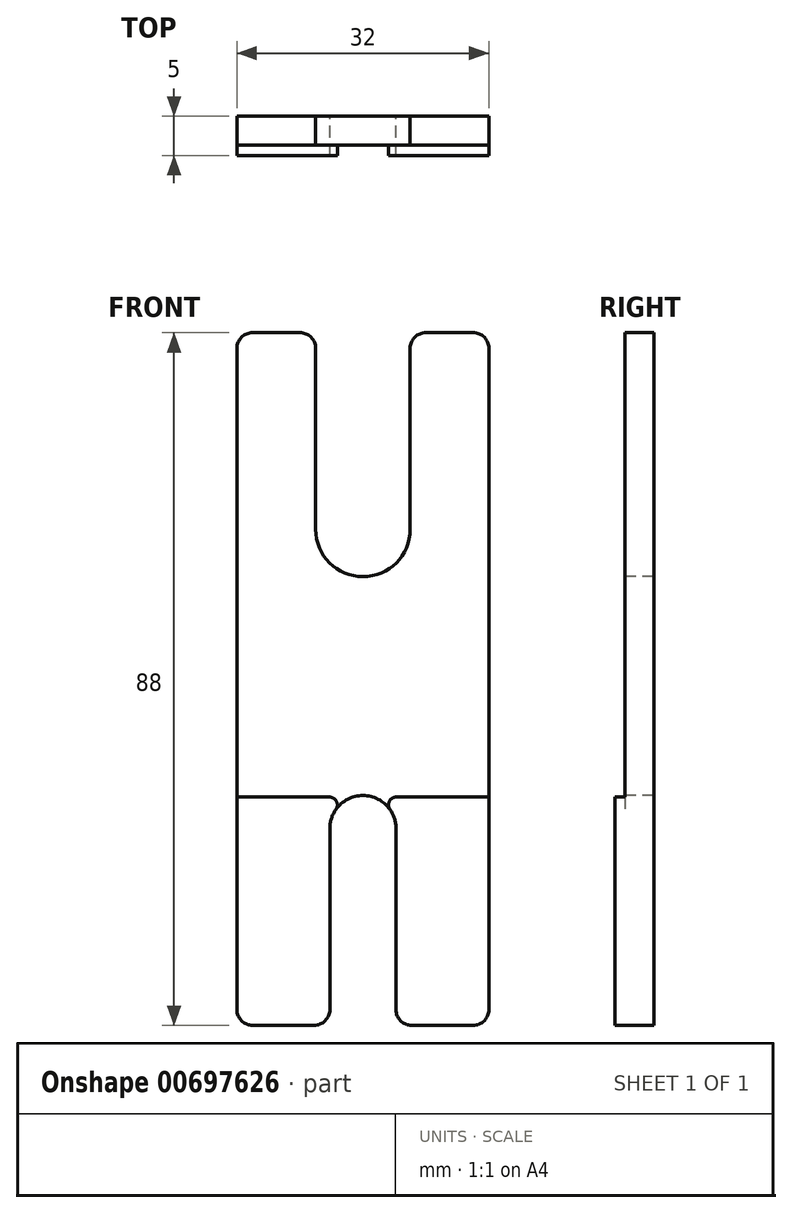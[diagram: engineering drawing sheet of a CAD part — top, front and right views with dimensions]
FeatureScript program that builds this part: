
annotation { "Feature Type Name" : "Feature", "Feature Type Description" : "" }
export const myFeature = defineFeature(function(context is Context, id is Id, definition is map)
    precondition{}
    {
        {
            var Q0;
            Q0=qCreatedBy(makeId("Front.planeOp"),FACE);
            cPlane(context, id + "F0", {"entities" : qUnion([Q0]), "cplaneType" : CPlaneType.OFFSET, "offset" : 13 * mm, "width" : 150 * mm, "height" : 150 * mm});
        }
        {
            var Q0;
            Q0=qCreatedBy(id+"F0.planeOp",FACE);
            var sketch = newSketch(context, id + "F1", { "sketchPlane" : qUnion([Q0])});
            skLineSegment(sketch, "E0.bottom", {"start": v(7, 75) * mm, "end": v(17, 75) * mm});
            skLineSegment(sketch, "E0.top", {"start": v(7, -13) * mm, "end": v(18.8, -13) * mm});
            skLineSegment(sketch, "E0.left", {"start": v(7, 75) * mm, "end": v(7, -13) * mm});
            skLineSegment(sketch, "E0.right", {"start": v(39, 75) * mm, "end": v(39, -13) * mm});
            skLineSegment(sketch, "E1", {"start": v(23, 75) * mm, "end": v(23, -13) * mm, "construction": true});
            skLineSegment(sketch, "E2", {"start": v(7, 31) * mm, "end": v(39, 31) * mm, "construction": true});
            skLineSegment(sketch, "E3", {"start": v(17, 75) * mm, "end": v(17, 50) * mm});
            skLineSegment(sketch, "E4", {"start": v(17, 50) * mm, "end": v(29, 50) * mm});
            skLineSegment(sketch, "E5", {"start": v(29, 50) * mm, "end": v(29, 75) * mm});
            skLineSegment(sketch, "E6", {"start": v(18.8, -13) * mm, "end": v(18.8, 12) * mm});
            skLineSegment(sketch, "E7", {"start": v(18.8, 12) * mm, "end": v(27.2, 12) * mm});
            skLineSegment(sketch, "E8", {"start": v(27.2, 12) * mm, "end": v(27.2, -13) * mm});
            skLineSegment(sketch, "E9.trimOffspring", {"start": v(27.2, -13) * mm, "end": v(39, -13) * mm});
            skLineSegment(sketch, "E10.trimOffspring", {"start": v(29, 75) * mm, "end": v(39, 75) * mm});
            skSolve(sketch);
        }
        {
            var Q0;
            Q0 = qSketchRegion(id + "F1", true);
            extrude(context, id + "F2", {"entities" : qUnion([Q0]), "depth" : (4 + 1) * mm, "offsetDistance" : 25 * mm});
        }
        {
            var Q0;
            Q0=makeQuery(id+"F2.opExtrude","CAP_FACE",FACE,{"disambiguationData":[OSD([sQuery(id+"F1.wireOp",EDGE,"E0.bottom"),sQuery(id+"F1.wireOp",EDGE,"E0.top"),sQuery(id+"F1.wireOp",EDGE,"E0.left"),sQuery(id+"F1.wireOp",EDGE,"E0.right"),sQuery(id+"F1.wireOp",EDGE,"E3"),sQuery(id+"F1.wireOp",EDGE,"E4"),sQuery(id+"F1.wireOp",EDGE,"E5"),sQuery(id+"F1.wireOp",EDGE,"E6"),sQuery(id+"F1.wireOp",EDGE,"E7"),sQuery(id+"F1.wireOp",EDGE,"E8"),sQuery(id+"F1.wireOp",EDGE,"E9.trimOffspring"),sQuery(id+"F1.wireOp",EDGE,"E10.trimOffspring")])],"isStart":false});
            cPlane(context, id + "F3", {"entities" : qUnion([Q0]), "cplaneType" : CPlaneType.OFFSET, "offset" : 0 * mm, "width" : 150 * mm, "height" : 150 * mm});
        }
        {
            var Q0;
            Q0=qCreatedBy(id+"F3.planeOp",FACE);
            var sketch = newSketch(context, id + "F4", { "sketchPlane" : qUnion([Q0])});
            skLineSegment(sketch, "E11.0.2", {"start": v(39, 16) * mm, "end": v(39, 75) * mm});
            skLineSegment(sketch, "E11.0.3", {"start": v(39, 75) * mm, "end": v(29, 75) * mm});
            skLineSegment(sketch, "E11.0.4", {"start": v(29, 75) * mm, "end": v(29, 50) * mm});
            skLineSegment(sketch, "E11.0.5", {"start": v(29, 50) * mm, "end": v(17, 50) * mm});
            skLineSegment(sketch, "E11.0.6", {"start": v(17, 50) * mm, "end": v(17, 75) * mm});
            skLineSegment(sketch, "E11.0.7", {"start": v(17, 75) * mm, "end": v(7, 75) * mm});
            skLineSegment(sketch, "E11.0.8", {"start": v(7, 75) * mm, "end": v(7, 16) * mm});
            skLineSegment(sketch, "E12", {"start": v(7, 16) * mm, "end": v(39, 16) * mm});
            skSolve(sketch);
        }
        {
            var Q0;
            Q0 = qSketchRegion(id + "F4", true);
            extrude(context, id + "F5", {"entities" : qUnion([Q0]), "operationType" : NewBodyOperationType.REMOVE, "oppositeDirection" : true, "depth" : (0.8 + 0.5) * mm, "offsetDistance" : 25 * mm});
        }
        {
            var Q0;
            Q0=makeQuery(id+"F2.opExtrude","CAP_FACE",FACE,{"disambiguationData":[OSD([sQuery(id+"F1.wireOp",EDGE,"E0.bottom"),sQuery(id+"F1.wireOp",EDGE,"E0.top"),sQuery(id+"F1.wireOp",EDGE,"E0.left"),sQuery(id+"F1.wireOp",EDGE,"E0.right"),sQuery(id+"F1.wireOp",EDGE,"E3"),sQuery(id+"F1.wireOp",EDGE,"E4"),sQuery(id+"F1.wireOp",EDGE,"E5"),sQuery(id+"F1.wireOp",EDGE,"E6"),sQuery(id+"F1.wireOp",EDGE,"E7"),sQuery(id+"F1.wireOp",EDGE,"E8"),sQuery(id+"F1.wireOp",EDGE,"E9.trimOffspring"),sQuery(id+"F1.wireOp",EDGE,"E10.trimOffspring")])],"isStart":false});
            cPlane(context, id + "F6", {"entities" : qUnion([Q0]), "cplaneType" : CPlaneType.OFFSET, "offset" : 0 * mm, "width" : 150 * mm, "height" : 150 * mm});
        }
        {
            var Q0;
            Q0=qCreatedBy(id+"F6.planeOp",FACE);
            var sketch = newSketch(context, id + "F7", { "sketchPlane" : qUnion([Q0])});
            skCircle(sketch, "E13", {"center": v(23, 50) * mm, "radius": 6 * mm});
            skCircle(sketch, "E14", {"center": v(23, 12) * mm, "radius": 4.2 * mm});
            skSolve(sketch);
        }
        {
            var Q0;
            Q0 = qSketchRegion(id + "F7", true);
            extrude(context, id + "F8", {"entities" : qUnion([Q0]), "operationType" : NewBodyOperationType.REMOVE, "endBound" : BoundingType.THROUGH_ALL, "oppositeDirection" : true, "depth" : 25 * mm, "offsetDistance" : 25 * mm});
        }
        {
            var Q0;
            Q0=makeQuery(id+"F2.opExtrude","SWEPT_EDGE",EDGE,{"disambiguationData":[OSD([sQuery(id+"F1.wireOp",EDGE,"E0.bottom"),sQuery(id+"F1.wireOp",EDGE,"E0.left")])]});
            var Q1;
            Q1=makeQuery(id+"F2.opExtrude","SWEPT_EDGE",EDGE,{"disambiguationData":[OSD([sQuery(id+"F1.wireOp",EDGE,"E0.bottom"),sQuery(id+"F1.wireOp",EDGE,"E3")])]});
            var Q2;
            Q2=makeQuery(id+"F2.opExtrude","SWEPT_EDGE",EDGE,{"disambiguationData":[OSD([sQuery(id+"F1.wireOp",EDGE,"E5"),sQuery(id+"F1.wireOp",EDGE,"E10.trimOffspring")])]});
            var Q3;
            Q3=makeQuery(id+"F2.opExtrude","SWEPT_EDGE",EDGE,{"disambiguationData":[OSD([sQuery(id+"F1.wireOp",EDGE,"E0.right"),sQuery(id+"F1.wireOp",EDGE,"E10.trimOffspring")])]});
            var Q4;
            Q4=makeQuery(id+"F2.opExtrude","SWEPT_EDGE",EDGE,{"disambiguationData":[OSD([sQuery(id+"F1.wireOp",EDGE,"E0.top"),sQuery(id+"F1.wireOp",EDGE,"E0.left")])]});
            var Q5;
            Q5=makeQuery(id+"F2.opExtrude","SWEPT_EDGE",EDGE,{"disambiguationData":[OSD([sQuery(id+"F1.wireOp",EDGE,"E0.top"),sQuery(id+"F1.wireOp",EDGE,"E6")])]});
            var Q6;
            Q6=makeQuery(id+"F2.opExtrude","SWEPT_EDGE",EDGE,{"disambiguationData":[OSD([sQuery(id+"F1.wireOp",EDGE,"E8"),sQuery(id+"F1.wireOp",EDGE,"E9.trimOffspring")])]});
            var Q7;
            Q7=makeQuery(id+"F2.opExtrude","SWEPT_EDGE",EDGE,{"disambiguationData":[OSD([sQuery(id+"F1.wireOp",EDGE,"E0.right"),sQuery(id+"F1.wireOp",EDGE,"E9.trimOffspring")])]});
            fillet(context, id + "F9", {"entities" : qUnion([Q0, Q1, Q2, Q3, Q4, Q5, Q6, Q7]), "radius" : 2 * mm, "tangentPropagation" : true, "allowEdgeOverflow" : false});
        }
        {
            var Q0;
            Q0=makeQuery(id+"F8.boolean.opBoolean","INTERSECT",EDGE,{"disambiguationData":[OD(1.0)],"derivedFrom":[makeQuery(id+"F5.boolean.opBoolean","COPY",FACE,{"derivedFrom":makeQuery(id+"F5.opExtrude","SWEPT_FACE",FACE,{"disambiguationData":[OSD([sQuery(id+"F4.wireOp",EDGE,"E12")])]})}),makeQuery(id+"F8.opExtrude","SWEPT_FACE",FACE,{"disambiguationData":[OSD([sQuery(id+"F7.wireOp",EDGE,"E14")])]})]});
            var Q1;
            Q1=makeQuery(id+"F8.boolean.opBoolean","INTERSECT",EDGE,{"disambiguationData":[OD(0.0)],"derivedFrom":[makeQuery(id+"F5.boolean.opBoolean","COPY",FACE,{"derivedFrom":makeQuery(id+"F5.opExtrude","SWEPT_FACE",FACE,{"disambiguationData":[OSD([sQuery(id+"F4.wireOp",EDGE,"E12")])]})}),makeQuery(id+"F8.opExtrude","SWEPT_FACE",FACE,{"disambiguationData":[OSD([sQuery(id+"F7.wireOp",EDGE,"E14")])]})]});
            fillet(context, id + "F10", {"entities" : qUnion([Q0, Q1]), "radius" : 1 * mm, "tangentPropagation" : true, "allowEdgeOverflow" : false});
        }
    });
